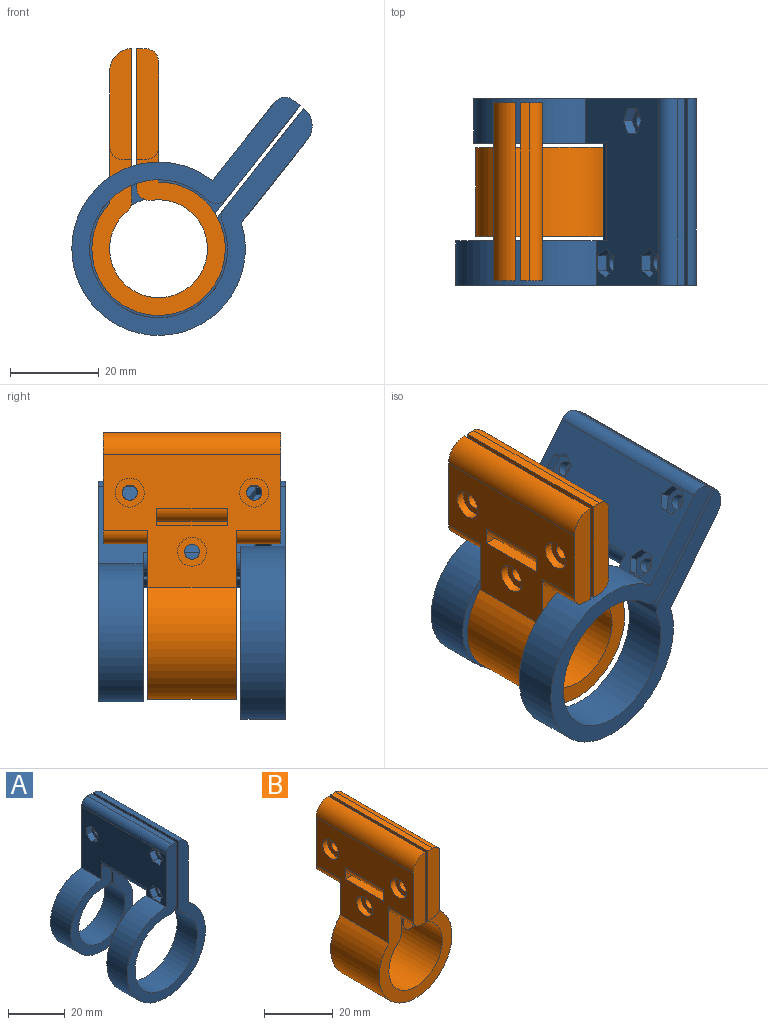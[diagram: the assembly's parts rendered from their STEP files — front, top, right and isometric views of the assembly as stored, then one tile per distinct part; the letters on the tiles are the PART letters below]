
ASSEMBLY  parts=2 mates=1
PART A: 61 faces, bbox 39x42x64.5 mm
  f0: plane 42x29.08mm, normal (1,0,0), area 748.9mm2, adj f1,f3,f6,f9,f12,f13,f15,f16
  f1: cylinder r=5mm len=42mm, axis (0,-1,0), area 321mm2, adj f0,f7,f9,f15,f54
  f2: plane 42x26.5mm, normal (-1,0,0), area 826.5mm2, adj f3,f6,f9,f12,f13,f15,f24,f25
  f3: plane 42.5x39mm, normal (0,1,0), area 452.2mm2, adj f0,f2,f4,f6,f7,f8,f10,f11
  f4: plane 42x30.64mm, normal (1,0,0), area 1095.2mm2, adj f3,f5,f9,f10,f12,f15,f21,f27
  f5: plane 42x2mm, normal (0,0,1), area 84mm2, adj f4,f9,f15,f25
  f6: cylinder r=19.5mm len=39mm, axis (0,1,0), area 1108.3mm2, adj f0,f2,f3,f9
  f7: plane 42x33.63mm, normal (-1,0,0), area 1131.4mm2, adj f1,f3,f9,f11,f12,f15,f16,f17
  f8: cylinder r=15.5mm len=31mm, axis (0,1,0), area 911.9mm2, adj f3,f9,f26,f27
  f9: plane 64.5x39mm, normal (0,-1,0), area 691.1mm2, adj f0,f1,f2,f4,f5,f6,f7,f8
  f10: plane 22x2mm, normal (0,0,-1), area 44mm2, adj f3,f4,f12,f24
  f11: plane 22x2mm, normal (0,0,-1), area 44mm2, adj f3,f7,f12,f23
  f12: plane 38.5x31mm, normal (0,-1,0), area 394.8mm2, adj f0,f2,f4,f7,f10,f11,f13,f14
  f13: cylinder r=15.5mm len=31mm, axis (0,-1,0), area 851.6mm2, adj f0,f2,f12,f15
  f14: cylinder r=11.5mm len=23mm, axis (0,-1,0), area 661.5mm2, adj f12,f15,f21,f22
  f15: plane 60.5x31mm, normal (0,1,0), area 633.6mm2, adj f0,f1,f2,f4,f5,f7,f13,f14
  f16: plane 5x4mm, normal (0,-1,0), area 6.9mm2, adj f0,f7,f17,f18,f20
  f17: plane 16x5mm, normal (0,0,1), area 80mm2, adj f0,f7,f16,f19
  f18: plane 16x2mm, normal (0,0,-1), area 32mm2, adj f7,f16,f19,f20
  f19: plane 5x4mm, normal (0,1,0), area 6.9mm2, adj f0,f7,f17,f18,f20
  f20: cylinder r=3mm len=16mm, axis (0,1,0), area 75.4mm2, adj f0,f16,f18,f19
  f21: cylinder r=3mm len=10mm, axis (0,-1,0), area 51.3mm2, adj f4,f12,f14,f15
  f22: cylinder r=3mm len=10mm, axis (0,-1,0), area 27mm2, adj f7,f12,f14,f15
  f23: cylinder r=3mm len=22mm, axis (0,1,0), area 103.7mm2, adj f0,f3,f11,f12
  f24: cylinder r=3mm len=22mm, axis (0,-1,0), area 103.7mm2, adj f2,f3,f10,f12
  f25: cylinder r=3mm len=42mm, axis (0,1,0), area 197.9mm2, adj f2,f5,f9,f15
  f26: cylinder r=3mm len=10mm, axis (0,1,0), area 31.9mm2, adj f3,f7,f8,f9
  f27: cylinder r=3mm len=10mm, axis (0,1,0), area 50.4mm2, adj f3,f4,f8,f9
  f28: plane 2.8x2.5mm, normal (0,-0.87,-0.5), area 8.1mm2, adj f2,f29,f33,f34
  f29: plane 2.8x2.5mm, normal (0,-0.87,0.5), area 8.1mm2, adj f2,f28,f30,f34
  f30: plane 3.23x2.5mm, normal (0,0,1), area 8.1mm2, adj f2,f29,f31,f34
  f31: plane 2.8x2.5mm, normal (0,0.87,0.5), area 8.1mm2, adj f2,f30,f32,f34
  f32: plane 2.8x2.5mm, normal (0,0.87,-0.5), area 8.1mm2, adj f2,f31,f33,f34
  f33: plane 3.23x2.5mm, normal (0,0,-1), area 8.1mm2, adj f2,f28,f32,f34
  f34: plane 6.47x5.6mm, normal (-1,0,0), area 18.1mm2, adj f28,f29,f30,f31,f32,f33,f51
  f35: plane 2.8x2.5mm, normal (0,0.5,-0.87), area 8.1mm2, adj f2,f36,f40,f41
  f36: plane 2.8x2.5mm, normal (0,-0.5,-0.87), area 8.1mm2, adj f2,f35,f37,f41
  f37: plane 3.23x2.5mm, normal (0,-1,0), area 8.1mm2, adj f2,f36,f38,f41
  f38: plane 2.8x2.5mm, normal (0,-0.5,0.87), area 8.1mm2, adj f2,f37,f39,f41
  f39: plane 2.8x2.5mm, normal (0,0.5,0.87), area 8.1mm2, adj f2,f38,f40,f41
  f40: plane 3.23x2.5mm, normal (0,1,0), area 8.1mm2, adj f2,f35,f39,f41
  f41: plane 6.47x5.6mm, normal (-1,0,0), area 18.1mm2, adj f35,f36,f37,f38,f39,f40,f50
  f42: plane 3.23x2.5mm, normal (0,0,1), area 8.1mm2, adj f2,f43,f47,f48
  f43: plane 2.8x2.5mm, normal (0,0.87,0.5), area 8.1mm2, adj f2,f42,f44,f48
  f44: plane 2.8x2.5mm, normal (0,0.87,-0.5), area 8.1mm2, adj f2,f43,f45,f48
  f45: plane 3.23x2.5mm, normal (0,0,-1), area 8.1mm2, adj f2,f44,f46,f48
  f46: plane 2.8x2.5mm, normal (0,-0.87,-0.5), area 8.1mm2, adj f2,f45,f47,f48
  f47: plane 2.8x2.5mm, normal (0,-0.87,0.5), area 8.1mm2, adj f2,f42,f46,f48
  f48: plane 6.47x5.6mm, normal (-1,0,0), area 18.1mm2, adj f42,f43,f44,f45,f46,f47,f49
  f49: cylinder r=1.7mm len=3.4mm, axis (1,0,0), area 26.7mm2, adj f4,f48
  f50: cylinder r=1.7mm len=3.4mm, axis (1,0,0), area 26.7mm2, adj f4,f41
  f51: cylinder r=1.7mm len=3.4mm, axis (1,0,0), area 26.7mm2, adj f4,f34
  f52: cylinder r=1.7mm len=3.4mm, axis (1,0,0), area 32mm2, adj f7,f53
  f53: plane 6.5x6.5mm, normal (1,0,0), area 24.1mm2, adj f52,f54
  f54: cylinder r=3.25mm len=6.5mm, axis (1,0,0), area 39.2mm2, adj f0,f1,f53
  f55: cylinder r=1.7mm len=3.4mm, axis (1,0,0), area 32mm2, adj f7,f56
  f56: plane 6.5x6.5mm, normal (1,0,0), area 24.1mm2, adj f55,f57
  f57: cylinder r=3.25mm len=6.5mm, axis (1,0,0), area 40.8mm2, adj f0,f56
  f58: cylinder r=1.7mm len=3.4mm, axis (1,0,0), area 32mm2, adj f7,f59
  f59: plane 6.5x6.5mm, normal (1,0,0), area 24.1mm2, adj f58,f60
  f60: cylinder r=3.25mm len=6.5mm, axis (1,0,0), area 40.8mm2, adj f0,f59
PART B: 63 faces, bbox 30x40x60 mm
  f0: plane 40x27mm, normal (1,0,0), area 838.5mm2, adj f1,f2,f8,f16,f18,f24,f25,f29
  f1: plane 38x30mm, normal (0,1,0), area 387.8mm2, adj f0,f4,f5,f6,f7,f8,f17,f19
  f2: plane 38x30mm, normal (0,-1,0), area 387.8mm2, adj f0,f4,f5,f6,f7,f8,f13,f15
  f3: plane 40x2mm, normal (0,0,1), area 80mm2, adj f4,f16,f18,f29
  f4: plane 40x31.14mm, normal (-1,0,0), area 1095.6mm2, adj f1,f2,f3,f15,f16,f17,f18,f27
  f5: cylinder r=11mm len=22mm, axis (0,-1,0), area 1260.2mm2, adj f1,f2,f27,f28
  f6: plane 40x34.28mm, normal (1,0,0), area 1142.5mm2, adj f1,f2,f9,f10,f11,f12,f13,f14
  f7: plane 40x29.8mm, normal (-1,0,0), area 773.2mm2, adj f1,f2,f8,f9,f11,f12,f14,f20
  f8: cylinder r=15mm len=30mm, axis (0,-1,0), area 1638mm2, adj f0,f1,f2,f7
  f9: plane 5x4mm, normal (0,-1,0), area 6.9mm2, adj f6,f7,f10,f11,f22
  f10: plane 15.83x2mm, normal (0,0,-1), area 31.7mm2, adj f6,f9,f12,f22
  f11: plane 15.83x5mm, normal (0,0,1), area 79.2mm2, adj f6,f7,f9,f12
  f12: plane 5x4mm, normal (0,1,0), area 6.9mm2, adj f6,f7,f10,f11,f22
  f13: plane 10x2mm, normal (0,0,-1), area 20mm2, adj f2,f6,f14,f26
  f14: plane 25x5mm, normal (0,-1,0), area 117.7mm2, adj f6,f7,f13,f21,f26
  f15: plane 10x2mm, normal (0,0,-1), area 20mm2, adj f2,f4,f16,f25
  f16: plane 25x5mm, normal (0,-1,0), area 121.1mm2, adj f0,f3,f4,f15,f25,f29
  f17: plane 10x2mm, normal (0,0,-1), area 20mm2, adj f1,f4,f18,f24
  f18: plane 25x5mm, normal (0,1,0), area 121.1mm2, adj f0,f3,f4,f17,f24,f29
  f19: plane 10x2mm, normal (0,0,-1), area 20mm2, adj f1,f6,f20,f23
  f20: plane 25x5mm, normal (0,1,0), area 117.7mm2, adj f6,f7,f19,f21,f23
  f21: cylinder r=5mm len=40mm, axis (0,-1,0), area 314.2mm2, adj f6,f7,f14,f20
  f22: cylinder r=3mm len=15.83mm, axis (0,1,0), area 74.6mm2, adj f7,f9,f10,f12
  f23: cylinder r=3mm len=10mm, axis (0,-1,0), area 47.1mm2, adj f1,f7,f19,f20
  f24: cylinder r=3mm len=10mm, axis (0,1,0), area 47.1mm2, adj f0,f1,f17,f18
  f25: cylinder r=3mm len=10mm, axis (0,1,0), area 47.1mm2, adj f0,f2,f15,f16
  f26: cylinder r=3mm len=10mm, axis (0,-1,0), area 47.1mm2, adj f2,f7,f13,f14
  f27: cylinder r=3mm len=20mm, axis (0,-1,0), area 102.8mm2, adj f1,f2,f4,f5
  f28: cylinder r=3mm len=20mm, axis (0,-1,0), area 52.4mm2, adj f1,f2,f5,f6
  f29: cylinder r=3mm len=40mm, axis (0,-1,0), area 188.5mm2, adj f0,f3,f16,f18
  f30: plane 2.8x2.5mm, normal (0,0.5,-0.87), area 8.1mm2, adj f0,f31,f35,f36
  f31: plane 3.23x2.5mm, normal (0,1,0), area 8.1mm2, adj f0,f30,f32,f36
  f32: plane 2.8x2.5mm, normal (0,0.5,0.87), area 8.1mm2, adj f0,f31,f33,f36
  f33: plane 2.8x2.5mm, normal (0,-0.5,0.87), area 8.1mm2, adj f0,f32,f34,f36
  f34: plane 3.23x2.5mm, normal (0,-1,0), area 8.1mm2, adj f0,f33,f35,f36
  f35: plane 2.8x2.5mm, normal (0,-0.5,-0.87), area 8.1mm2, adj f0,f30,f34,f36
  f36: plane 6.47x5.6mm, normal (1,0,0), area 18.1mm2, adj f30,f31,f32,f33,f34,f35,f53
  f37: plane 3.23x2.5mm, normal (0,0,-1), area 8.1mm2, adj f0,f38,f42,f43
  f38: plane 2.8x2.5mm, normal (0,0.87,-0.5), area 8.1mm2, adj f0,f37,f39,f43
  f39: plane 2.8x2.5mm, normal (0,0.87,0.5), area 8.1mm2, adj f0,f38,f40,f43
  f40: plane 3.23x2.5mm, normal (0,0,1), area 8.1mm2, adj f0,f39,f41,f43
  f41: plane 2.8x2.5mm, normal (0,-0.87,0.5), area 8.1mm2, adj f0,f40,f42,f43
  f42: plane 2.8x2.5mm, normal (0,-0.87,-0.5), area 8.1mm2, adj f0,f37,f41,f43
  f43: plane 6.47x5.6mm, normal (1,0,0), area 18.1mm2, adj f37,f38,f39,f40,f41,f42,f52
  f44: plane 2.8x2.5mm, normal (0,-0.5,0.87), area 8.1mm2, adj f0,f45,f49,f50
  f45: plane 3.23x2.5mm, normal (0,-1,0), area 8.1mm2, adj f0,f44,f46,f50
  f46: plane 2.8x2.5mm, normal (0,-0.5,-0.87), area 8.1mm2, adj f0,f45,f47,f50
  f47: plane 2.8x2.5mm, normal (0,0.5,-0.87), area 8.1mm2, adj f0,f46,f48,f50
  f48: plane 3.23x2.5mm, normal (0,1,0), area 8.1mm2, adj f0,f47,f49,f50
  f49: plane 2.8x2.5mm, normal (0,0.5,0.87), area 8.1mm2, adj f0,f44,f48,f50
  f50: plane 6.47x5.6mm, normal (1,0,0), area 18.1mm2, adj f44,f45,f46,f47,f48,f49,f51
  f51: cylinder r=1.7mm len=3.4mm, axis (-1,0,0), area 26.7mm2, adj f4,f50
  f52: cylinder r=1.7mm len=3.4mm, axis (-1,0,0), area 26.7mm2, adj f4,f43
  f53: cylinder r=1.7mm len=3.4mm, axis (-1,0,0), area 26.7mm2, adj f4,f36
  f54: cylinder r=1.7mm len=3.4mm, axis (-1,0,0), area 32mm2, adj f6,f55
  f55: plane 6.5x6.5mm, normal (-1,0,0), area 24.1mm2, adj f54,f56
  f56: cylinder r=3.25mm len=6.5mm, axis (-1,0,0), area 40.8mm2, adj f7,f55
  f57: cylinder r=1.7mm len=3.4mm, axis (-1,0,0), area 32mm2, adj f6,f58
  f58: plane 6.5x6.5mm, normal (-1,0,0), area 24.1mm2, adj f57,f59
  f59: cylinder r=3.25mm len=6.5mm, axis (-1,0,0), area 40.8mm2, adj f7,f58
  f60: cylinder r=1.7mm len=3.4mm, axis (-1,0,0), area 32mm2, adj f6,f61
  f61: plane 6.5x6.5mm, normal (-1,0,0), area 24.1mm2, adj f60,f62
  f62: cylinder r=3.25mm len=6.5mm, axis (-1,0,0), area 40.8mm2, adj f7,f61
PLACE A rot(axis=(0,1,0),38.4deg) t=(0,-2,0)mm
PLACE B rot(axis=(0,1,0),0deg) t=(0,-1,0)mm fixed
MATE revolute B.f5 <-> A.f8  axis (0,-1,0) through (0,-1,0)mm
